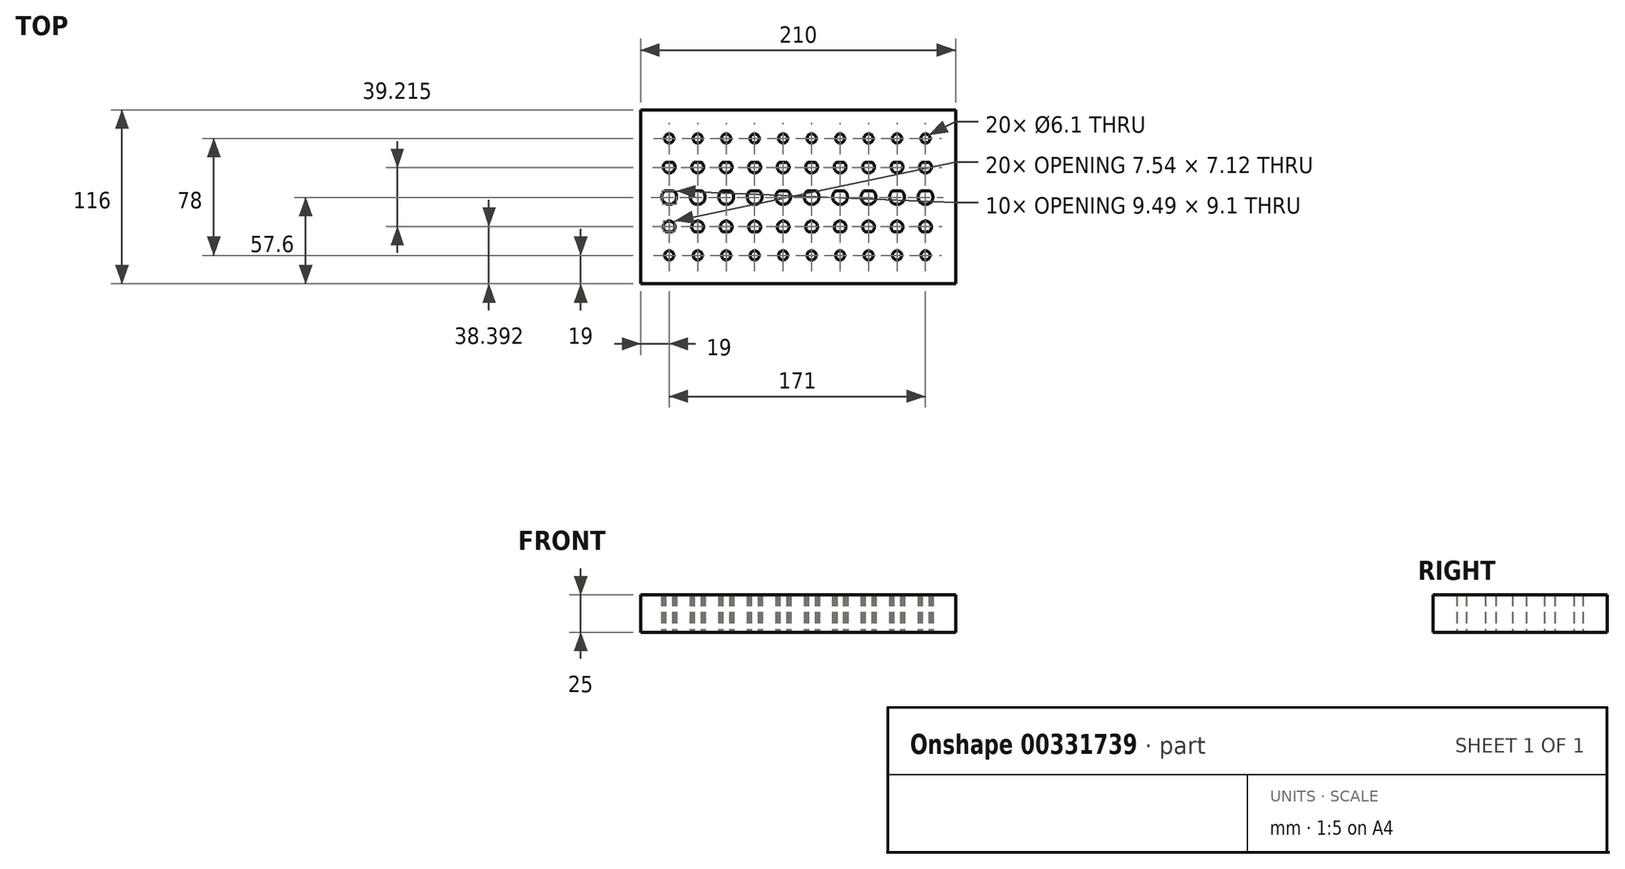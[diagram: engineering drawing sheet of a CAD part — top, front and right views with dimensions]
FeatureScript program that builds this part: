
annotation { "Feature Type Name" : "Feature", "Feature Type Description" : "" }
export const myFeature = defineFeature(function(context is Context, id is Id, definition is map)
    precondition{}
    {
        {
            var Q0;
            Q0=qCreatedBy(makeId("Top.planeOp"),FACE);
            var sketch = newSketch(context, id + "F0", { "sketchPlane" : qUnion([Q0])});
            skLineSegment(sketch, "E0.bottom", {"start": v(0, 0) * mm, "end": v(210, 0) * mm});
            skLineSegment(sketch, "E0.top", {"start": v(0, 116) * mm, "end": v(210, 116) * mm});
            skLineSegment(sketch, "E0.left", {"start": v(0, 0) * mm, "end": v(0, 116) * mm});
            skLineSegment(sketch, "E0.right", {"start": v(210, 0) * mm, "end": v(210, 116) * mm});
            skLineSegment(sketch, "E1.bottom", {"start": v(4, 4) * mm, "end": v(206, 4) * mm});
            skLineSegment(sketch, "E1.top", {"start": v(4, 112) * mm, "end": v(206, 112) * mm});
            skLineSegment(sketch, "E1.left", {"start": v(4, 4) * mm, "end": v(4, 112) * mm});
            skLineSegment(sketch, "E1.right", {"start": v(206, 4) * mm, "end": v(206, 112) * mm});
            skLineSegment(sketch, "E2", {"start": v(105, 112) * mm, "end": v(105, 116) * mm, "construction": true});
            skLineSegment(sketch, "E3", {"start": v(4, 58) * mm, "end": v(0, 58) * mm, "construction": true});
            skLineSegment(sketch, "E4", {"start": v(206, 58) * mm, "end": v(210, 58) * mm, "construction": true});
            skPoint(sketch, "E5.endSnap0", {"position": v(105, 0) * mm});
            skLineSegment(sketch, "E6", {"start": v(105, 0) * mm, "end": v(105, 4) * mm, "construction": true});
            skSolve(sketch);
        }
        {
            var Q0;
            Q0=makeQuery(id+"F0.imprint","IMPRINT",FACE,{"disambiguationData":[TD([[makeQuery(id+"F0.imprint","IMPRINT",EDGE,{"derivedFrom":sQuery(id+"F0.wireOp",EDGE,"E1.bottom")}),1.0]])]});
            var sketch = newSketch(context, id + "F1", { "sketchPlane" : qUnion([Q0])});
            skLineSegment(sketch, "E7.bottom", {"start": v(0, 0) * mm, "end": v(210, 0) * mm});
            skLineSegment(sketch, "E7.top", {"start": v(0, 116) * mm, "end": v(210, 116) * mm});
            skLineSegment(sketch, "E7.left", {"start": v(0, 0) * mm, "end": v(0, 116) * mm});
            skLineSegment(sketch, "E7.right", {"start": v(210, 0) * mm, "end": v(210, 116) * mm});
            skCircle(sketch, "E8", {"center": v(19, 97) * mm, "radius": 3.05 * mm});
            skArc(sketch, "E9", {"start": v(16.64, 81.17) * mm, "mid": v(19, 74.05) * mm, "end": v(21.36, 81.17) * mm});
            skLineSegment(sketch, "E10", {"start": v(0, 58) * mm, "end": v(210, 58) * mm, "construction": true});
            skArc(sketch, "E11", {"start": v(16.3, 62.15) * mm, "mid": v(19, 53.05) * mm, "end": v(21.7, 62.15) * mm});
            skLineSegment(sketch, "E12", {"start": v(16.3, 62.15) * mm, "end": v(21.7, 62.15) * mm});
            skLineSegment(sketch, "E13", {"start": v(16.64, 81.17) * mm, "end": v(21.36, 81.17) * mm});
            skPoint(sketch, "E14.orphan", {"position": v(19, 74.07) * mm});
            skArc(sketch, "E15.MirrorCS", {"start": v(16.64, 34.83) * mm, "mid": v(19, 41.95) * mm, "end": v(21.36, 34.83) * mm});
            skLineSegment(sketch, "E16.MirrorCS", {"start": v(16.64, 34.83) * mm, "end": v(21.36, 34.83) * mm});
            skCircle(sketch, "E17.MirrorC", {"center": v(19, 19) * mm, "radius": 3.05 * mm});
            skCircle(sketch, "E18.1.0.0", {"center": v(38, 97) * mm, "radius": 3.05 * mm});
            skPoint(sketch, "E18.1.0.1", {"position": v(38, 74.07) * mm});
            skArc(sketch, "E18.1.0.2", {"start": v(35.64, 34.83) * mm, "mid": v(38, 41.95) * mm, "end": v(40.36, 34.83) * mm});
            skArc(sketch, "E18.1.0.3", {"start": v(35.3, 62.15) * mm, "mid": v(38, 53.05) * mm, "end": v(40.7, 62.15) * mm});
            skCircle(sketch, "E18.1.0.4", {"center": v(38, 19) * mm, "radius": 3.05 * mm});
            skLineSegment(sketch, "E18.1.0.6", {"start": v(35.3, 62.15) * mm, "end": v(40.7, 62.15) * mm});
            skLineSegment(sketch, "E18.1.0.7", {"start": v(35.64, 81.17) * mm, "end": v(40.36, 81.17) * mm});
            skArc(sketch, "E18.1.0.8", {"start": v(35.64, 81.17) * mm, "mid": v(38, 74.05) * mm, "end": v(40.36, 81.17) * mm});
            skLineSegment(sketch, "E18.1.0.9", {"start": v(35.64, 34.83) * mm, "end": v(40.36, 34.83) * mm});
            skCircle(sketch, "E18.2.0.0", {"center": v(57, 97) * mm, "radius": 3.05 * mm});
            skPoint(sketch, "E18.2.0.1", {"position": v(57, 74.07) * mm});
            skArc(sketch, "E18.2.0.2", {"start": v(54.64, 34.83) * mm, "mid": v(57, 41.95) * mm, "end": v(59.36, 34.83) * mm});
            skArc(sketch, "E18.2.0.3", {"start": v(54.3, 62.15) * mm, "mid": v(57, 53.05) * mm, "end": v(59.7, 62.15) * mm});
            skCircle(sketch, "E18.2.0.4", {"center": v(57, 19) * mm, "radius": 3.05 * mm});
            skLineSegment(sketch, "E18.2.0.6", {"start": v(54.3, 62.15) * mm, "end": v(59.7, 62.15) * mm});
            skLineSegment(sketch, "E18.2.0.7", {"start": v(54.64, 81.17) * mm, "end": v(59.36, 81.17) * mm});
            skArc(sketch, "E18.2.0.8", {"start": v(54.64, 81.17) * mm, "mid": v(57, 74.05) * mm, "end": v(59.36, 81.17) * mm});
            skLineSegment(sketch, "E18.2.0.9", {"start": v(54.64, 34.83) * mm, "end": v(59.36, 34.83) * mm});
            skLineSegment(sketch, "E18.direction1", {"start": v(19, 19) * mm, "end": v(38, 19) * mm, "construction": true});
            skCircle(sketch, "E19.0.3.0", {"center": v(76, 97) * mm, "radius": 3.05 * mm});
            skPoint(sketch, "E19.2.3.0", {"position": v(76, 74.07) * mm});
            skArc(sketch, "E19.3.3.0", {"start": v(73.64, 34.83) * mm, "mid": v(76, 41.95) * mm, "end": v(78.36, 34.83) * mm});
            skArc(sketch, "E19.7.3.0", {"start": v(73.3, 62.15) * mm, "mid": v(76, 53.05) * mm, "end": v(78.7, 62.15) * mm});
            skCircle(sketch, "E19.11.3.0", {"center": v(76, 19) * mm, "radius": 3.05 * mm});
            skLineSegment(sketch, "E19.16.3.0", {"start": v(73.3, 62.15) * mm, "end": v(78.7, 62.15) * mm});
            skLineSegment(sketch, "E19.19.3.0", {"start": v(73.64, 81.17) * mm, "end": v(78.36, 81.17) * mm});
            skArc(sketch, "E19.22.3.0", {"start": v(73.64, 81.17) * mm, "mid": v(76, 74.05) * mm, "end": v(78.36, 81.17) * mm});
            skLineSegment(sketch, "E19.26.3.0", {"start": v(73.64, 34.83) * mm, "end": v(78.36, 34.83) * mm});
            skCircle(sketch, "E19.0.4.0", {"center": v(95, 97) * mm, "radius": 3.05 * mm});
            skPoint(sketch, "E19.2.4.0", {"position": v(95, 74.07) * mm});
            skArc(sketch, "E19.3.4.0", {"start": v(92.64, 34.83) * mm, "mid": v(95, 41.95) * mm, "end": v(97.36, 34.83) * mm});
            skArc(sketch, "E19.7.4.0", {"start": v(92.3, 62.15) * mm, "mid": v(95, 53.05) * mm, "end": v(97.7, 62.15) * mm});
            skCircle(sketch, "E19.11.4.0", {"center": v(95, 19) * mm, "radius": 3.05 * mm});
            skLineSegment(sketch, "E19.16.4.0", {"start": v(92.3, 62.15) * mm, "end": v(97.7, 62.15) * mm});
            skLineSegment(sketch, "E19.19.4.0", {"start": v(92.64, 81.17) * mm, "end": v(97.36, 81.17) * mm});
            skArc(sketch, "E19.22.4.0", {"start": v(92.64, 81.17) * mm, "mid": v(95, 74.05) * mm, "end": v(97.36, 81.17) * mm});
            skLineSegment(sketch, "E19.26.4.0", {"start": v(92.64, 34.83) * mm, "end": v(97.36, 34.83) * mm});
            skCircle(sketch, "E19.0.5.0", {"center": v(114, 97) * mm, "radius": 3.05 * mm});
            skPoint(sketch, "E19.2.5.0", {"position": v(114, 74.07) * mm});
            skArc(sketch, "E19.3.5.0", {"start": v(111.64, 34.83) * mm, "mid": v(114, 41.95) * mm, "end": v(116.36, 34.83) * mm});
            skArc(sketch, "E19.7.5.0", {"start": v(111.3, 62.15) * mm, "mid": v(114, 53.05) * mm, "end": v(116.7, 62.15) * mm});
            skCircle(sketch, "E19.11.5.0", {"center": v(114, 19) * mm, "radius": 3.05 * mm});
            skLineSegment(sketch, "E19.16.5.0", {"start": v(111.3, 62.15) * mm, "end": v(116.7, 62.15) * mm});
            skLineSegment(sketch, "E19.19.5.0", {"start": v(111.64, 81.17) * mm, "end": v(116.36, 81.17) * mm});
            skArc(sketch, "E19.22.5.0", {"start": v(111.64, 81.17) * mm, "mid": v(114, 74.05) * mm, "end": v(116.36, 81.17) * mm});
            skLineSegment(sketch, "E19.26.5.0", {"start": v(111.64, 34.83) * mm, "end": v(116.36, 34.83) * mm});
            skCircle(sketch, "E19.0.6.0", {"center": v(133, 97) * mm, "radius": 3.05 * mm});
            skPoint(sketch, "E19.2.6.0", {"position": v(133, 74.07) * mm});
            skArc(sketch, "E19.3.6.0", {"start": v(130.64, 34.83) * mm, "mid": v(133, 41.95) * mm, "end": v(135.36, 34.83) * mm});
            skArc(sketch, "E19.7.6.0", {"start": v(130.3, 62.15) * mm, "mid": v(133, 53.05) * mm, "end": v(135.7, 62.15) * mm});
            skCircle(sketch, "E19.11.6.0", {"center": v(133, 19) * mm, "radius": 3.05 * mm});
            skLineSegment(sketch, "E19.16.6.0", {"start": v(130.3, 62.15) * mm, "end": v(135.7, 62.15) * mm});
            skLineSegment(sketch, "E19.19.6.0", {"start": v(130.64, 81.17) * mm, "end": v(135.36, 81.17) * mm});
            skArc(sketch, "E19.22.6.0", {"start": v(130.64, 81.17) * mm, "mid": v(133, 74.05) * mm, "end": v(135.36, 81.17) * mm});
            skLineSegment(sketch, "E19.26.6.0", {"start": v(130.64, 34.83) * mm, "end": v(135.36, 34.83) * mm});
            skCircle(sketch, "E19.0.7.0", {"center": v(152, 97) * mm, "radius": 3.05 * mm});
            skPoint(sketch, "E19.2.7.0", {"position": v(152, 74.07) * mm});
            skArc(sketch, "E19.3.7.0", {"start": v(149.64, 34.83) * mm, "mid": v(152, 41.95) * mm, "end": v(154.36, 34.83) * mm});
            skArc(sketch, "E19.7.7.0", {"start": v(149.3, 62.15) * mm, "mid": v(152, 53.05) * mm, "end": v(154.7, 62.15) * mm});
            skCircle(sketch, "E19.11.7.0", {"center": v(152, 19) * mm, "radius": 3.05 * mm});
            skLineSegment(sketch, "E19.16.7.0", {"start": v(149.3, 62.15) * mm, "end": v(154.7, 62.15) * mm});
            skLineSegment(sketch, "E19.19.7.0", {"start": v(149.64, 81.17) * mm, "end": v(154.36, 81.17) * mm});
            skArc(sketch, "E19.22.7.0", {"start": v(149.64, 81.17) * mm, "mid": v(152, 74.05) * mm, "end": v(154.36, 81.17) * mm});
            skLineSegment(sketch, "E19.26.7.0", {"start": v(149.64, 34.83) * mm, "end": v(154.36, 34.83) * mm});
            skCircle(sketch, "E19.0.8.0", {"center": v(171, 97) * mm, "radius": 3.05 * mm});
            skPoint(sketch, "E19.2.8.0", {"position": v(171, 74.07) * mm});
            skArc(sketch, "E19.3.8.0", {"start": v(168.64, 34.83) * mm, "mid": v(171, 41.95) * mm, "end": v(173.36, 34.83) * mm});
            skArc(sketch, "E19.7.8.0", {"start": v(168.3, 62.15) * mm, "mid": v(171, 53.05) * mm, "end": v(173.7, 62.15) * mm});
            skCircle(sketch, "E19.11.8.0", {"center": v(171, 19) * mm, "radius": 3.05 * mm});
            skLineSegment(sketch, "E19.16.8.0", {"start": v(168.3, 62.15) * mm, "end": v(173.7, 62.15) * mm});
            skLineSegment(sketch, "E19.19.8.0", {"start": v(168.64, 81.17) * mm, "end": v(173.36, 81.17) * mm});
            skArc(sketch, "E19.22.8.0", {"start": v(168.64, 81.17) * mm, "mid": v(171, 74.05) * mm, "end": v(173.36, 81.17) * mm});
            skLineSegment(sketch, "E19.26.8.0", {"start": v(168.64, 34.83) * mm, "end": v(173.36, 34.83) * mm});
            skCircle(sketch, "E19.0.9.0", {"center": v(190, 97) * mm, "radius": 3.05 * mm});
            skPoint(sketch, "E19.2.9.0", {"position": v(190, 74.07) * mm});
            skArc(sketch, "E19.3.9.0", {"start": v(187.64, 34.83) * mm, "mid": v(190, 41.95) * mm, "end": v(192.36, 34.83) * mm});
            skArc(sketch, "E19.7.9.0", {"start": v(187.3, 62.15) * mm, "mid": v(190, 53.05) * mm, "end": v(192.7, 62.15) * mm});
            skCircle(sketch, "E19.11.9.0", {"center": v(190, 19) * mm, "radius": 3.05 * mm});
            skLineSegment(sketch, "E19.16.9.0", {"start": v(187.3, 62.15) * mm, "end": v(192.7, 62.15) * mm});
            skLineSegment(sketch, "E19.19.9.0", {"start": v(187.64, 81.17) * mm, "end": v(192.36, 81.17) * mm});
            skArc(sketch, "E19.22.9.0", {"start": v(187.64, 81.17) * mm, "mid": v(190, 74.05) * mm, "end": v(192.36, 81.17) * mm});
            skLineSegment(sketch, "E19.26.9.0", {"start": v(187.64, 34.83) * mm, "end": v(192.36, 34.83) * mm});
            skSolve(sketch);
        }
        {
            var Q0;
            Q0 = qSketchRegion(id + "F1", true);
            extrude(context, id + "F2", {"entities" : qUnion([Q0]), "depth" : 25 * mm});
        }
    });
